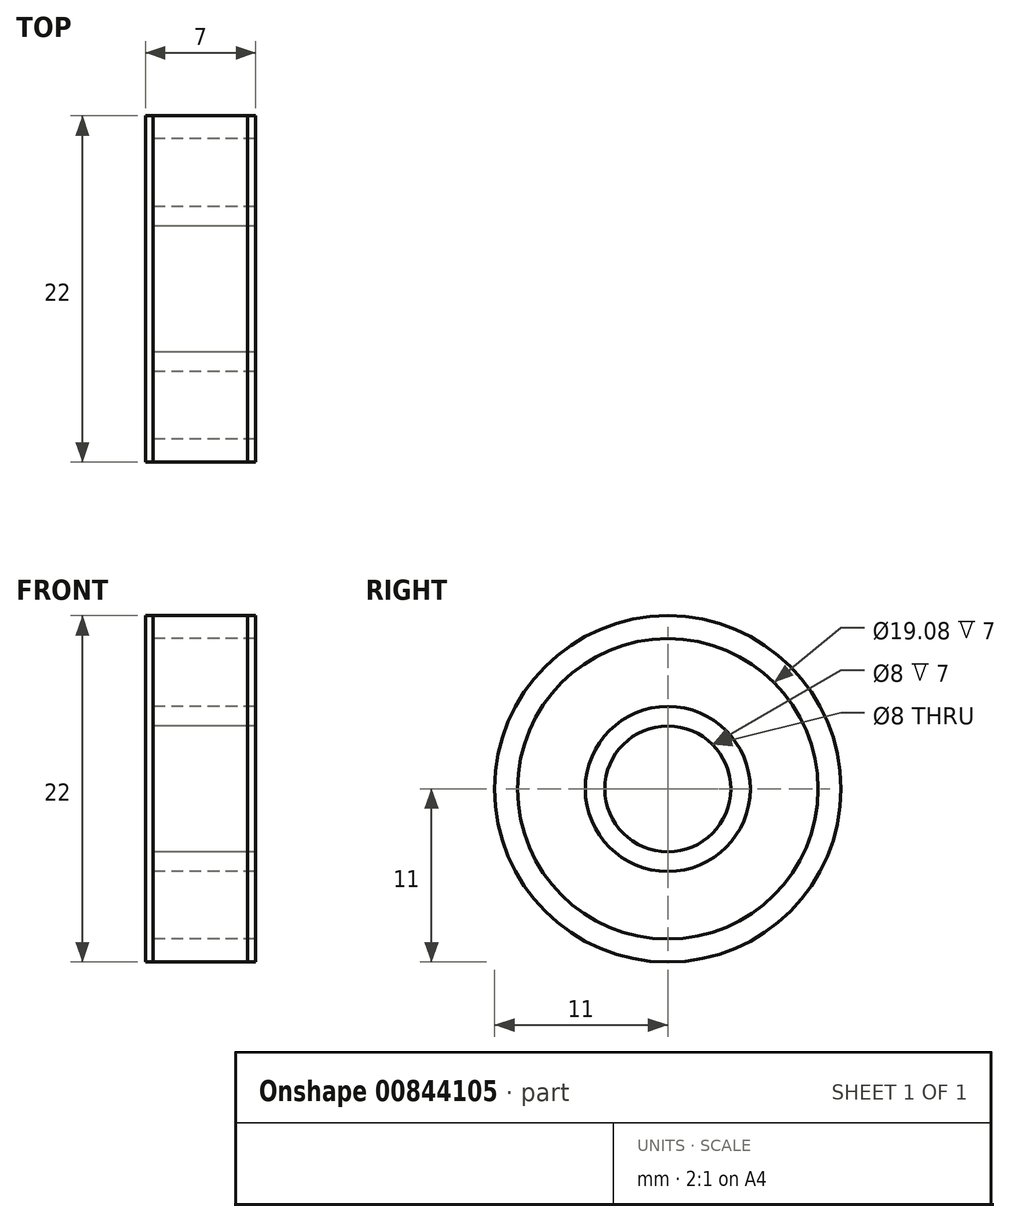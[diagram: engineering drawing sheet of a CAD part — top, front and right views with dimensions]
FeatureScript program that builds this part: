
annotation { "Feature Type Name" : "Feature", "Feature Type Description" : "" }
export const myFeature = defineFeature(function(context is Context, id is Id, definition is map)
    precondition{}
    {
        {
            var Q0;
            Q0=qCreatedBy(makeId("Right.planeOp"),FACE);
            var sketch = newSketch(context, id + "F0", { "sketchPlane" : qUnion([Q0])});
            skCircle(sketch, "E0", {"center": v(0, 0) * mm, "radius": 4 * mm});
            skCircle(sketch, "E1", {"center": v(0, 0) * mm, "radius": 11 * mm});
            skSolve(sketch);
        }
        {
            var Q0;
            Q0=makeQuery(id+"F0.imprint","IMPRINT",FACE,{"disambiguationData":[TD([[makeQuery(id+"F0.imprint","IMPRINT",EDGE,{"derivedFrom":sQuery(id+"F0.wireOp",EDGE,"E0")}),-1.0]])]});
            extrude(context, id + "F1", {"entities" : qUnion([Q0]), "endBound" : BoundingType.SYMMETRIC, "depth" : 6 * mm, "offsetDistance" : 25.4 * mm});
        }
        {
            var Q0;
            Q0=qCreatedBy(makeId("Right.planeOp"),FACE);
            var sketch = newSketch(context, id + "F2", { "sketchPlane" : qUnion([Q0])});
            skCircle(sketch, "E2", {"center": v(0, 0) * mm, "radius": 11 * mm});
            skCircle(sketch, "E3", {"center": v(0, 0) * mm, "radius": 4 * mm});
            skCircle(sketch, "E4", {"center": v(0, 0) * mm, "radius": 5.24 * mm});
            skCircle(sketch, "E5", {"center": v(0, 0) * mm, "radius": 9.54 * mm});
            skSolve(sketch);
        }
        {
            var Q0;
            Q0=makeQuery(id+"F2.imprint","IMPRINT",FACE,{"disambiguationData":[TD([[makeQuery(id+"F2.imprint","IMPRINT",EDGE,{"derivedFrom":sQuery(id+"F2.wireOp",EDGE,"E2")}),1.0]])]});
            var Q1;
            Q1=makeQuery(id+"F2.imprint","IMPRINT",FACE,{"disambiguationData":[TD([[makeQuery(id+"F2.imprint","IMPRINT",EDGE,{"derivedFrom":sQuery(id+"F2.wireOp",EDGE,"E3")}),-1.0]])]});
            extrude(context, id + "F3", {"entities" : qUnion([Q0, Q1]), "endBound" : BoundingType.SYMMETRIC, "depth" : 7 * mm, "offsetDistance" : 25.4 * mm});
        }
    });
